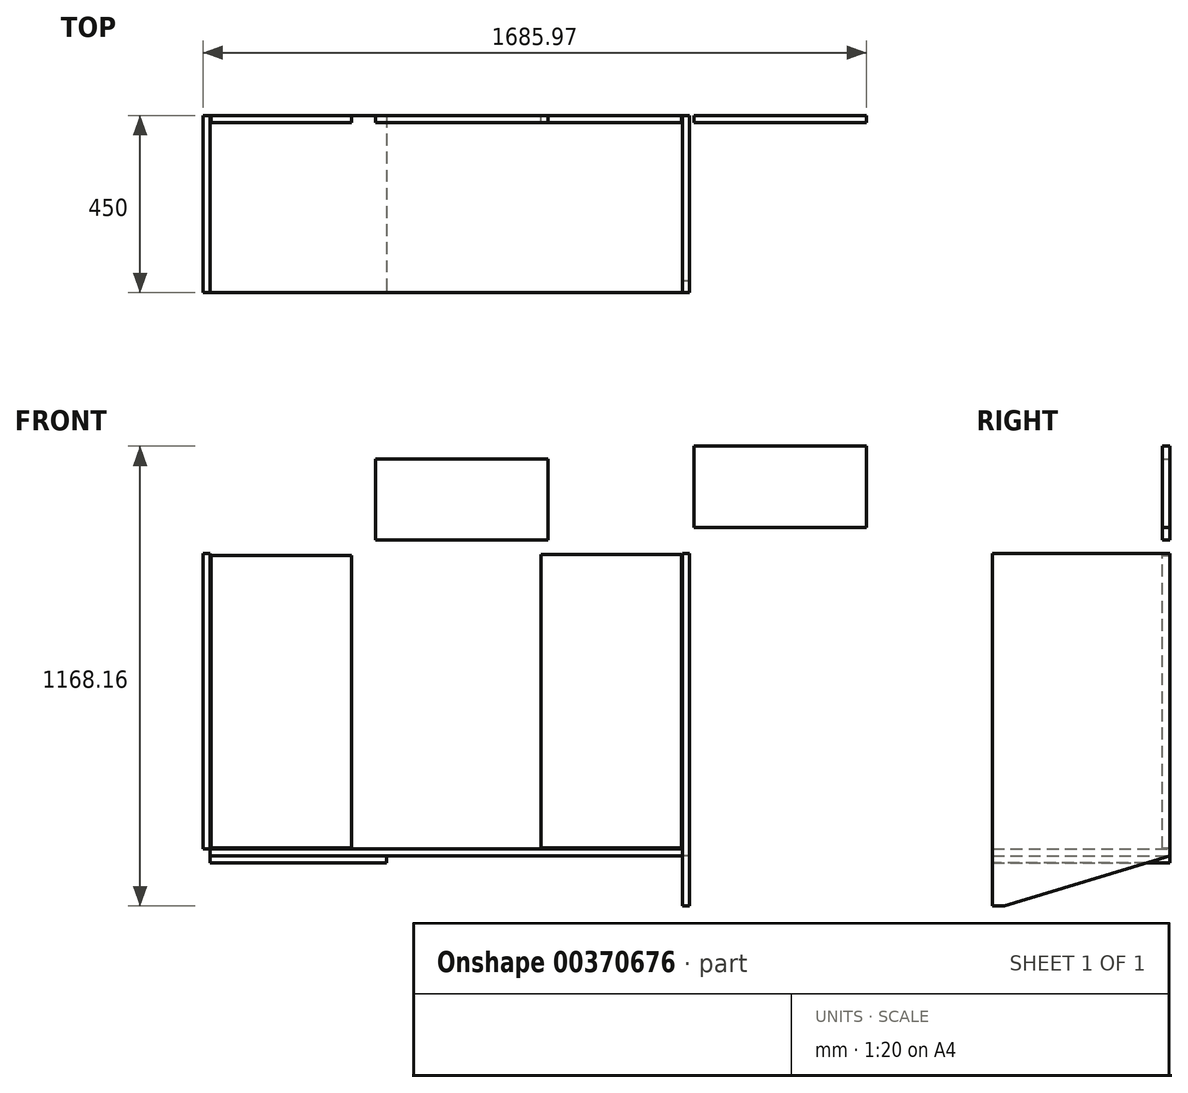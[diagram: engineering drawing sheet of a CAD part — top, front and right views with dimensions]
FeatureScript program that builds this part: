
annotation { "Feature Type Name" : "Feature", "Feature Type Description" : "" }
export const myFeature = defineFeature(function(context is Context, id is Id, definition is map)
    precondition{}
    {
        {
            var Q0;
            Q0=qCreatedBy(makeId("Top.planeOp"),FACE);
            var sketch = newSketch(context, id + "F0", { "sketchPlane" : qUnion([Q0])});
            skLineSegment(sketch, "E0.bottom", {"start": v(600, -225) * mm, "end": v(-600, -225) * mm});
            skLineSegment(sketch, "E0.top", {"start": v(600, 225) * mm, "end": v(-600, 225) * mm});
            skLineSegment(sketch, "E0.left", {"start": v(600, -225) * mm, "end": v(600, 225) * mm});
            skLineSegment(sketch, "E0.right", {"start": v(-600, -225) * mm, "end": v(-600, 225) * mm});
            skPoint(sketch, "E0.middle", {"position": v(0, 0) * mm});
            skSolve(sketch);
        }
        {
            var Q0;
            Q0 = qSketchRegion(id + "F0", true);
            extrude(context, id + "F1", {"entities" : qUnion([Q0]), "depth" : 18 * mm});
        }
        {
            var Q0;
            Q0=makeQuery(id+"F1.opExtrude","SWEPT_FACE",FACE,{"disambiguationData":[OSD([sQuery(id+"F0.wireOp",EDGE,"E0.top")])]});
            var sketch = newSketch(context, id + "F2", { "sketchPlane" : qUnion([Q0])});
            skLineSegment(sketch, "E1.bottom", {"start": v(-598, 20) * mm, "end": v(-241, 20) * mm});
            skLineSegment(sketch, "E1.top", {"start": v(-598, 766) * mm, "end": v(-241, 766) * mm});
            skLineSegment(sketch, "E1.left", {"start": v(-598, 20) * mm, "end": v(-598, 766) * mm});
            skLineSegment(sketch, "E1.right", {"start": v(-241, 20) * mm, "end": v(-241, 766) * mm});
            skLineSegment(sketch, "E2.bottom", {"start": v(598, 20) * mm, "end": v(241, 20) * mm});
            skLineSegment(sketch, "E2.top", {"start": v(598, 764) * mm, "end": v(241, 764) * mm});
            skLineSegment(sketch, "E2.left", {"start": v(598, 20) * mm, "end": v(598, 764) * mm});
            skLineSegment(sketch, "E2.right", {"start": v(241, 18) * mm, "end": v(241, 764) * mm});
            skLineSegment(sketch, "E3.bottom", {"start": v(-1067.97, 1041.16) * mm, "end": v(-629.97, 1041.16) * mm});
            skLineSegment(sketch, "E3.top", {"start": v(-1067.97, 835.16) * mm, "end": v(-629.97, 835.16) * mm});
            skLineSegment(sketch, "E3.left", {"start": v(-1067.97, 1041.16) * mm, "end": v(-1067.97, 835.16) * mm});
            skLineSegment(sketch, "E3.right", {"start": v(-629.97, 1041.16) * mm, "end": v(-629.97, 835.16) * mm});
            skLineSegment(sketch, "E4.bottom", {"start": v(-258.08, 1008.52) * mm, "end": v(179.92, 1008.52) * mm});
            skLineSegment(sketch, "E4.top", {"start": v(-258.08, 802.52) * mm, "end": v(179.92, 802.52) * mm});
            skLineSegment(sketch, "E4.left", {"start": v(-258.08, 1008.52) * mm, "end": v(-258.08, 802.52) * mm});
            skLineSegment(sketch, "E4.right", {"start": v(179.92, 1008.52) * mm, "end": v(179.92, 802.52) * mm});
            skSolve(sketch);
        }
        {
            var Q0;
            Q0 = qSketchRegion(id + "F2", true);
            extrude(context, id + "F3", {"entities" : qUnion([Q0]), "oppositeDirection" : true, "depth" : 18 * mm});
        }
        {
            var Q0;
            Q0=makeQuery(id+"F1.opExtrude","SWEPT_FACE",FACE,{"disambiguationData":[OSD([sQuery(id+"F0.wireOp",EDGE,"E0.left")])]});
            var sketch = newSketch(context, id + "F4", { "sketchPlane" : qUnion([Q0])});
            skLineSegment(sketch, "E5", {"start": v(-225, -127) * mm, "end": v(-195, -127) * mm});
            skLineSegment(sketch, "E6", {"start": v(225, 0) * mm, "end": v(225, 768) * mm});
            skLineSegment(sketch, "E7", {"start": v(225, 768) * mm, "end": v(-225, 768) * mm});
            skLineSegment(sketch, "E8", {"start": v(-225, 768) * mm, "end": v(-225, -127) * mm});
            skLineSegment(sketch, "E9", {"start": v(-195, -127) * mm, "end": v(225, 0) * mm});
            skSolve(sketch);
        }
        {
            var Q0;
            Q0 = qSketchRegion(id + "F4", true);
            extrude(context, id + "F5", {"entities" : qUnion([Q0]), "depth" : 18 * mm});
        }
        {
            var Q0;
            Q0=makeQuery(id+"F1.opExtrude","SWEPT_FACE",FACE,{"disambiguationData":[OSD([sQuery(id+"F0.wireOp",EDGE,"E0.right")])]});
            var sketch = newSketch(context, id + "F6", { "sketchPlane" : qUnion([Q0])});
            skLineSegment(sketch, "E10.bottom", {"start": v(-225, 18) * mm, "end": v(225, 18) * mm});
            skLineSegment(sketch, "E10.top", {"start": v(-225, 768) * mm, "end": v(225, 768) * mm});
            skLineSegment(sketch, "E10.left", {"start": v(-225, 18) * mm, "end": v(-225, 768) * mm});
            skLineSegment(sketch, "E10.right", {"start": v(225, 18) * mm, "end": v(225, 768) * mm});
            skSolve(sketch);
        }
        {
            var Q0;
            Q0 = qSketchRegion(id + "F6", true);
            extrude(context, id + "F7", {"entities" : qUnion([Q0]), "depth" : 18 * mm});
        }
        {
            var Q0;
            Q0=makeQuery(id+"F1.opExtrude","CAP_FACE",FACE,{"disambiguationData":[OSD([sQuery(id+"F0.wireOp",EDGE,"E0.bottom"),sQuery(id+"F0.wireOp",EDGE,"E0.top"),sQuery(id+"F0.wireOp",EDGE,"E0.left"),sQuery(id+"F0.wireOp",EDGE,"E0.right")])],"isStart":true});
            var sketch = newSketch(context, id + "F8", { "sketchPlane" : qUnion([Q0])});
            skLineSegment(sketch, "E11.bottom", {"start": v(-600, -225) * mm, "end": v(-152, -225) * mm});
            skLineSegment(sketch, "E11.top", {"start": v(-600, 225) * mm, "end": v(-152, 225) * mm});
            skLineSegment(sketch, "E11.left", {"start": v(-600, -225) * mm, "end": v(-600, 225) * mm});
            skLineSegment(sketch, "E11.right", {"start": v(-152, -225) * mm, "end": v(-152, 225) * mm});
            skSolve(sketch);
        }
        {
            var Q0;
            Q0 = qSketchRegion(id + "F8", true);
            extrude(context, id + "F9", {"entities" : qUnion([Q0]), "depth" : 18 * mm});
        }
    });
